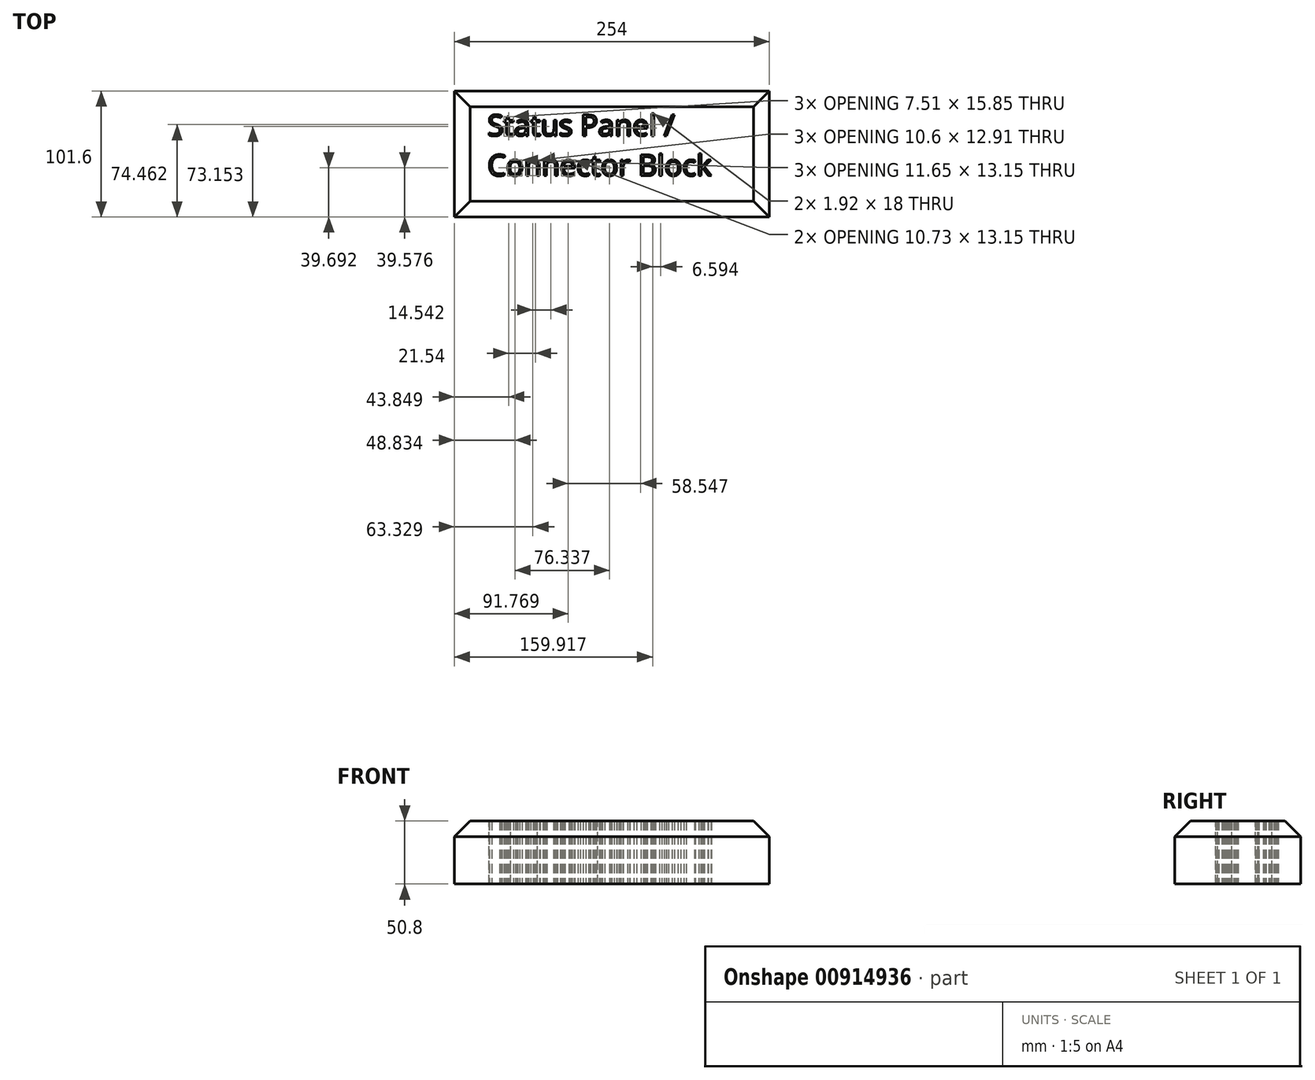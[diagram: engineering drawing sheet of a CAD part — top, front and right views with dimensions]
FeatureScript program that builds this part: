
annotation { "Feature Type Name" : "Feature", "Feature Type Description" : "" }
export const myFeature = defineFeature(function(context is Context, id is Id, definition is map)
    precondition{}
    {
        {
            var Q0;
            Q0=qCreatedBy(makeId("Top.planeOp"),FACE);
            var sketch = newSketch(context, id + "F0", { "sketchPlane" : qUnion([Q0])});
            skLineSegment(sketch, "E0.bottom", {"start": v(-117.75, 40.16) * mm, "end": v(136.25, 40.16) * mm});
            skLineSegment(sketch, "E0.top", {"start": v(-117.75, -61.44) * mm, "end": v(136.25, -61.44) * mm});
            skLineSegment(sketch, "E0.left", {"start": v(-117.75, 40.16) * mm, "end": v(-117.75, -61.44) * mm});
            skLineSegment(sketch, "E0.right", {"start": v(136.25, 40.16) * mm, "end": v(136.25, -61.44) * mm});
            skSolve(sketch);
        }
        {
            var Q0;
            Q0=makeQuery(id+"F0.imprint","IMPRINT",FACE,{"disambiguationData":[TD([[makeQuery(id+"F0.imprint","IMPRINT",EDGE,{"derivedFrom":sQuery(id+"F0.wireOp",EDGE,"E0.bottom")}),-1.0]])]});
            extrude(context, id + "F1", {"entities" : qUnion([Q0]), "depth" : 50.8 * mm, "offsetDistance" : 25.4 * mm});
        }
        {
            var Q0;
            Q0=qCreatedBy(makeId("Top.planeOp"),FACE);
            var sketch = newSketch(context, id + "F2", { "sketchPlane" : qUnion([Q0])});
            skText(sketch, "E1", { "text": "Status Panel /\nConnector Block", "fontName": "OpenSans-Regular.ttf"});
            const initialGuessF2  = {"E1": [-0.09102, 0.00402, 1, 0, 0.01706]};
            skSetInitialGuess(sketch, initialGuessF2);
            skSolve(sketch);
        }
        {
            var Q0;
            Q0 = qSketchRegion(id + "F2", true);
            extrude(context, id + "F3", {"entities" : qUnion([Q0]), "operationType" : NewBodyOperationType.REMOVE, "endBound" : BoundingType.THROUGH_ALL, "depth" : 25.4 * mm, "offsetDistance" : 25.4 * mm});
        }
        {
            var Q0;
            Q0=makeQuery(id+"F1.opExtrude","CAP_EDGE",EDGE,{"disambiguationData":[OSD([sQuery(id+"F0.wireOp",EDGE,"E0.bottom")])],"isStart":false});
            var Q1;
            Q1=makeQuery(id+"F1.opExtrude","CAP_EDGE",EDGE,{"disambiguationData":[OSD([sQuery(id+"F0.wireOp",EDGE,"E0.left")])],"isStart":false});
            var Q2;
            Q2=makeQuery(id+"F1.opExtrude","CAP_EDGE",EDGE,{"disambiguationData":[OSD([sQuery(id+"F0.wireOp",EDGE,"E0.top")])],"isStart":false});
            var Q3;
            Q3=makeQuery(id+"F1.opExtrude","CAP_EDGE",EDGE,{"disambiguationData":[OSD([sQuery(id+"F0.wireOp",EDGE,"E0.right")])],"isStart":false});
            chamfer(context, id + "F4", {"entities" : qUnion([Q0, Q1, Q2, Q3]), "width" : 12.7 * mm, "tangentPropagation" : true});
        }
    });
